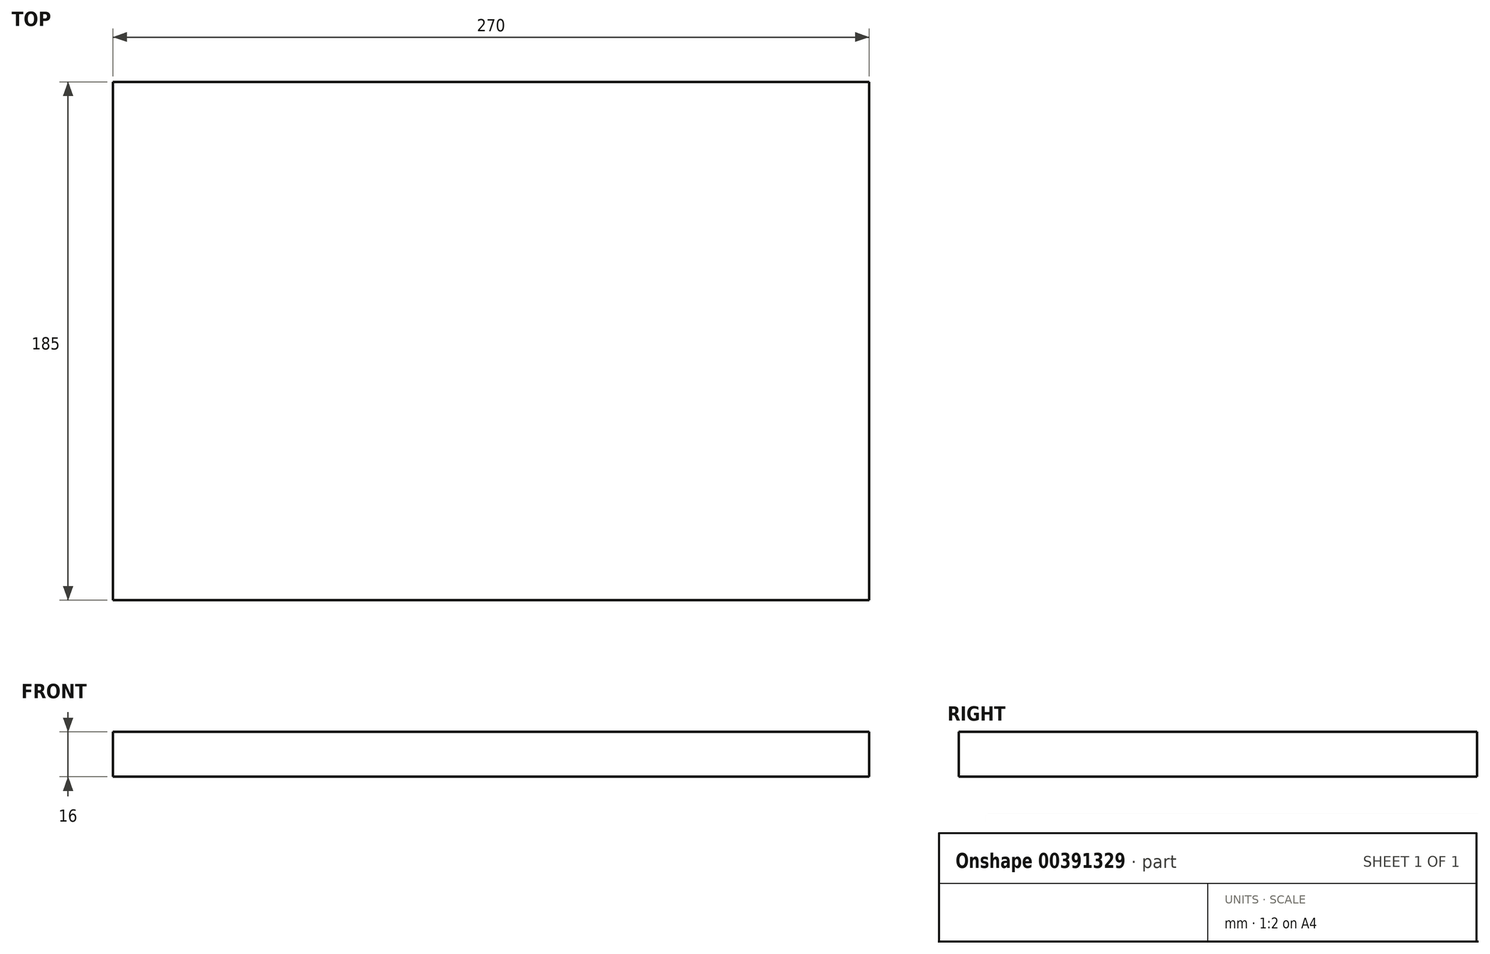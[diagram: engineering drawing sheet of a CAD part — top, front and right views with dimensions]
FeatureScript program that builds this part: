
annotation { "Feature Type Name" : "Feature", "Feature Type Description" : "" }
export const myFeature = defineFeature(function(context is Context, id is Id, definition is map)
    precondition{}
    {
        {
            var Q0;
            Q0=qCreatedBy(makeId("Top.planeOp"),FACE);
            var sketch = newSketch(context, id + "F0", { "sketchPlane" : qUnion([Q0])});
            skLineSegment(sketch, "E0.bottom", {"start": v(-135, 92.5) * mm, "end": v(135, 92.5) * mm});
            skLineSegment(sketch, "E0.top", {"start": v(-135, -92.5) * mm, "end": v(135, -92.5) * mm});
            skLineSegment(sketch, "E0.left", {"start": v(-135, 92.5) * mm, "end": v(-135, -92.5) * mm});
            skLineSegment(sketch, "E0.right", {"start": v(135, 92.5) * mm, "end": v(135, -92.5) * mm});
            skSolve(sketch);
        }
        {
            var Q0;
            Q0=qSketchRegion(id+"F0",true);
            extrude(context, id + "F1", {"entities" : qUnion([Q0]), "depth" : 16 * mm});
        }
    });
